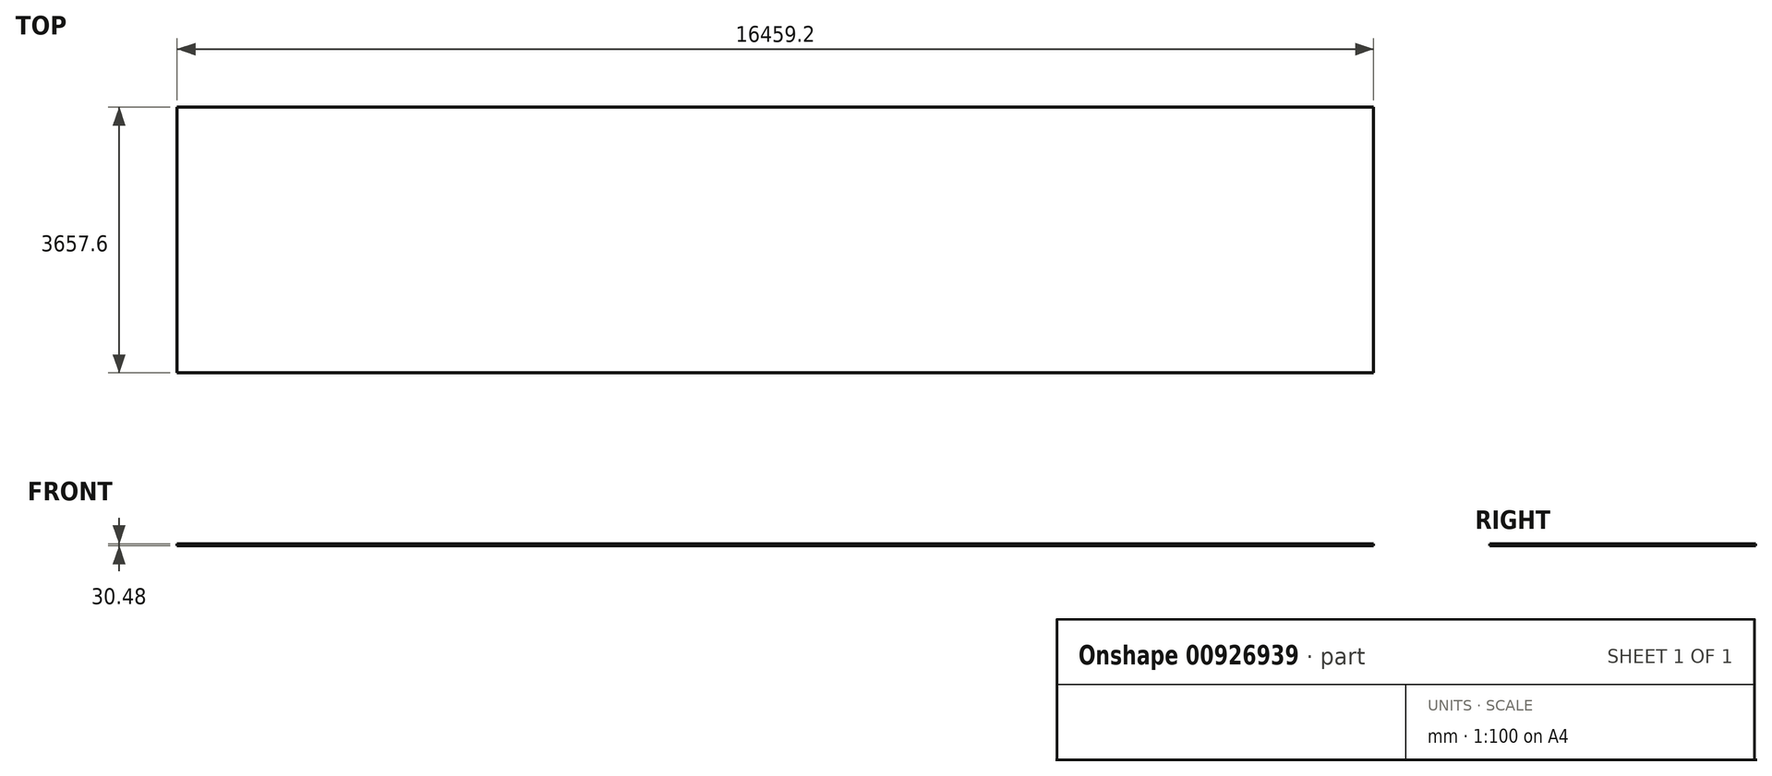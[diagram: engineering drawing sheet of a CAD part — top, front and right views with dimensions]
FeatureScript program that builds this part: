
annotation { "Feature Type Name" : "Feature", "Feature Type Description" : "" }
export const myFeature = defineFeature(function(context is Context, id is Id, definition is map)
    precondition{}
    {
        {
            var Q0;
            Q0=qCreatedBy(makeId("Top.planeOp"),FACE);
            var sketch = newSketch(context, id + "F0", { "sketchPlane" : qUnion([Q0])});
            skLineSegment(sketch, "E0.bottom", {"start": v(0, 0) * mm, "end": v(16459.2, 0) * mm});
            skLineSegment(sketch, "E0.top", {"start": v(0, -3657.6) * mm, "end": v(16459.2, -3657.6) * mm});
            skLineSegment(sketch, "E0.left", {"start": v(0, 0) * mm, "end": v(0, -3657.6) * mm});
            skLineSegment(sketch, "E0.right", {"start": v(16459.2, 0) * mm, "end": v(16459.2, -3657.6) * mm});
            skSolve(sketch);
        }
        {
            var Q0;
            Q0=makeQuery(id+"F0.imprint","IMPRINT",FACE,{"disambiguationData":[TD([[makeQuery(id+"F0.imprint","IMPRINT",EDGE,{"derivedFrom":sQuery(id+"F0.wireOp",EDGE,"E0.bottom")}),-1.0]])]});
            extrude(context, id + "F1", {"entities" : qUnion([Q0]), "depth" : 30.48 * mm, "offsetDistance" : 30.48 * mm});
        }
    });
